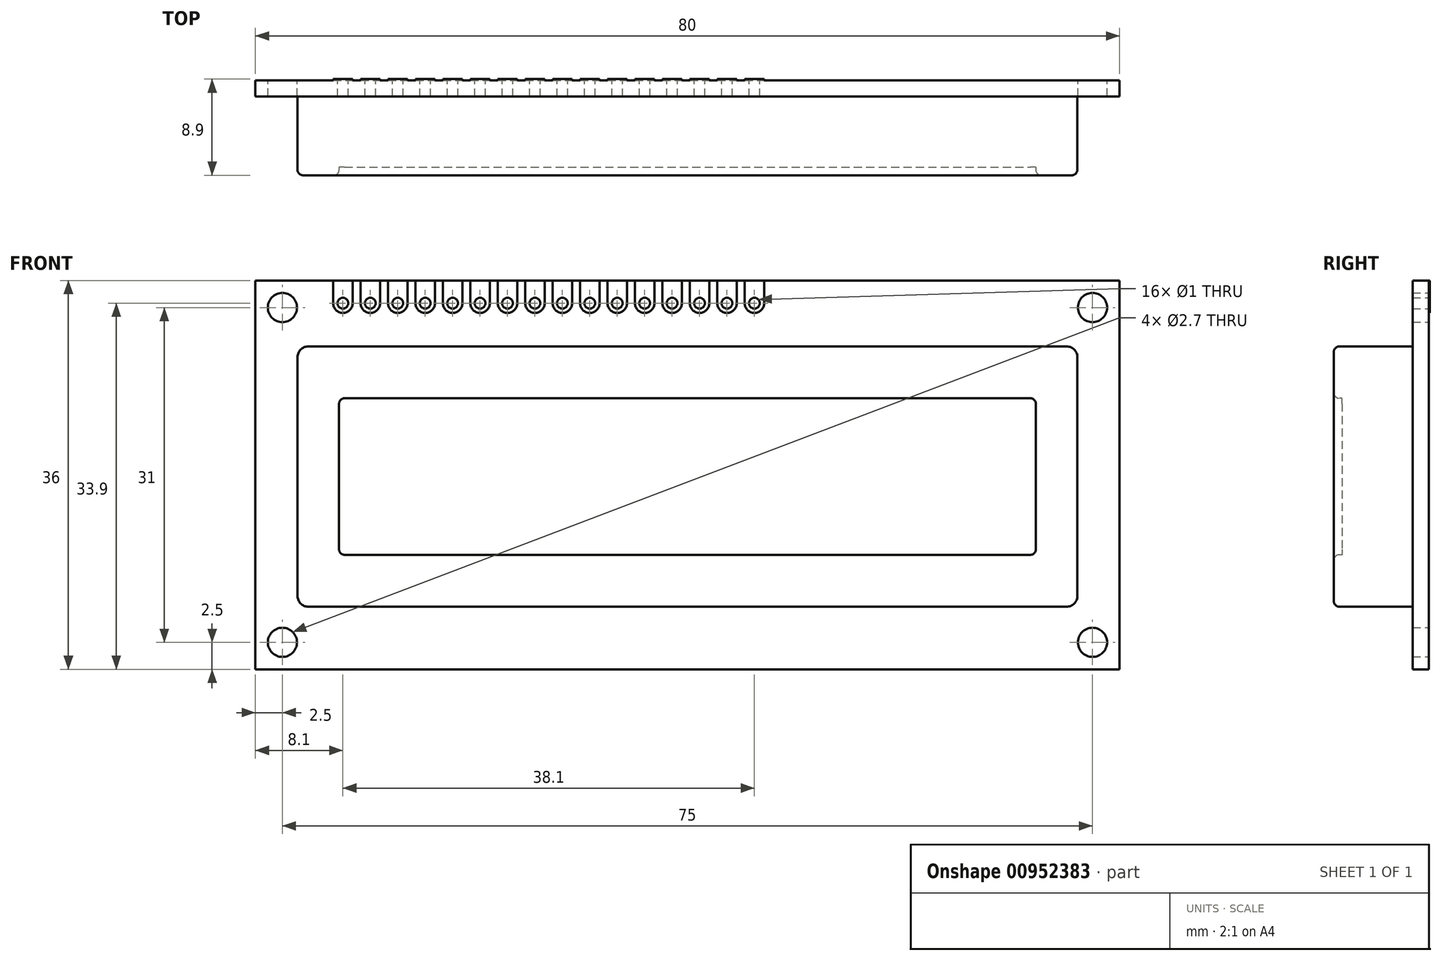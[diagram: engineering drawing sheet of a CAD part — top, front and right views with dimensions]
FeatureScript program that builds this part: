
annotation { "Feature Type Name" : "Feature", "Feature Type Description" : "" }
export const myFeature = defineFeature(function(context is Context, id is Id, definition is map)
    precondition{}
    {
        {
            var Q0;
            Q0=qCreatedBy(makeId("Front.planeOp"),FACE);
            var sketch = newSketch(context, id + "F0", { "sketchPlane" : qUnion([Q0])});
            skLineSegment(sketch, "E0.bottom", {"start": v(0, 0) * mm, "end": v(80, 0) * mm});
            skLineSegment(sketch, "E0.top", {"start": v(0, -36) * mm, "end": v(80, -36) * mm});
            skLineSegment(sketch, "E0.left", {"start": v(0, 0) * mm, "end": v(0, -36) * mm});
            skLineSegment(sketch, "E0.right", {"start": v(80, 0) * mm, "end": v(80, -36) * mm});
            skCircle(sketch, "E1", {"center": v(2.5, -2.5) * mm, "radius": 1.35 * mm});
            skCircle(sketch, "E2", {"center": v(77.5, -2.5) * mm, "radius": 1.35 * mm});
            skCircle(sketch, "E3", {"center": v(77.5, -33.5) * mm, "radius": 1.35 * mm});
            skCircle(sketch, "E4", {"center": v(2.5, -33.5) * mm, "radius": 1.35 * mm});
            skCircle(sketch, "E5", {"center": v(8.1, -2.1) * mm, "radius": 0.5 * mm});
            skCircle(sketch, "E6.1.0.0", {"center": v(10.64, -2.1) * mm, "radius": 0.5 * mm});
            skCircle(sketch, "E6.2.0.0", {"center": v(13.18, -2.1) * mm, "radius": 0.5 * mm});
            skCircle(sketch, "E6.3.0.0", {"center": v(15.72, -2.1) * mm, "radius": 0.5 * mm});
            skCircle(sketch, "E6.4.0.0", {"center": v(18.26, -2.1) * mm, "radius": 0.5 * mm});
            skCircle(sketch, "E6.5.0.0", {"center": v(20.8, -2.1) * mm, "radius": 0.5 * mm});
            skCircle(sketch, "E6.6.0.0", {"center": v(23.34, -2.1) * mm, "radius": 0.5 * mm});
            skCircle(sketch, "E6.7.0.0", {"center": v(25.88, -2.1) * mm, "radius": 0.5 * mm});
            skCircle(sketch, "E6.8.0.0", {"center": v(28.42, -2.1) * mm, "radius": 0.5 * mm});
            skCircle(sketch, "E6.9.0.0", {"center": v(30.96, -2.1) * mm, "radius": 0.5 * mm});
            skCircle(sketch, "E6.10.0.0", {"center": v(33.5, -2.1) * mm, "radius": 0.5 * mm});
            skCircle(sketch, "E6.11.0.0", {"center": v(36.04, -2.1) * mm, "radius": 0.5 * mm});
            skCircle(sketch, "E6.12.0.0", {"center": v(38.58, -2.1) * mm, "radius": 0.5 * mm});
            skCircle(sketch, "E6.13.0.0", {"center": v(41.12, -2.1) * mm, "radius": 0.5 * mm});
            skCircle(sketch, "E6.14.0.0", {"center": v(43.66, -2.1) * mm, "radius": 0.5 * mm});
            skCircle(sketch, "E6.15.0.0", {"center": v(46.2, -2.1) * mm, "radius": 0.5 * mm});
            skLineSegment(sketch, "E6.direction1", {"start": v(8.1, -2.1) * mm, "end": v(10.64, -2.1) * mm, "construction": true});
            skArc(sketch, "E7", {"start": v(7.2, -2.1) * mm, "mid": v(8.1, -3) * mm, "end": v(9, -2.1) * mm});
            skLineSegment(sketch, "E8", {"start": v(8.1, -2.1) * mm, "end": v(8.1, 0) * mm, "construction": true});
            skLineSegment(sketch, "E9", {"start": v(9, -2.1) * mm, "end": v(9, 0) * mm});
            skLineSegment(sketch, "E10", {"start": v(8.1, -2.1) * mm, "end": v(6.53, -2.1) * mm, "construction": true});
            skLineSegment(sketch, "E11", {"start": v(7.2, -2.1) * mm, "end": v(7.2, 0) * mm});
            skLineSegment(sketch, "E12", {"start": v(7.2, 0) * mm, "end": v(9, 0) * mm});
            skLineSegment(sketch, "E13.1.0.0", {"start": v(9.74, 0) * mm, "end": v(11.54, 0) * mm});
            skLineSegment(sketch, "E13.1.0.1", {"start": v(9.74, -2.1) * mm, "end": v(9.74, 0) * mm});
            skLineSegment(sketch, "E13.1.0.2", {"start": v(11.54, -2.1) * mm, "end": v(11.54, 0) * mm});
            skArc(sketch, "E13.1.0.3", {"start": v(9.74, -2.1) * mm, "mid": v(10.64, -3) * mm, "end": v(11.54, -2.1) * mm});
            skLineSegment(sketch, "E13.2.0.0", {"start": v(12.28, 0) * mm, "end": v(14.08, 0) * mm});
            skLineSegment(sketch, "E13.2.0.1", {"start": v(12.28, -2.1) * mm, "end": v(12.28, 0) * mm});
            skLineSegment(sketch, "E13.2.0.2", {"start": v(14.08, -2.1) * mm, "end": v(14.08, 0) * mm});
            skArc(sketch, "E13.2.0.3", {"start": v(12.28, -2.1) * mm, "mid": v(13.18, -3) * mm, "end": v(14.08, -2.1) * mm});
            skLineSegment(sketch, "E13.3.0.0", {"start": v(14.82, 0) * mm, "end": v(16.62, 0) * mm});
            skLineSegment(sketch, "E13.3.0.1", {"start": v(14.82, -2.1) * mm, "end": v(14.82, 0) * mm});
            skLineSegment(sketch, "E13.3.0.2", {"start": v(16.62, -2.1) * mm, "end": v(16.62, 0) * mm});
            skArc(sketch, "E13.3.0.3", {"start": v(14.82, -2.1) * mm, "mid": v(15.72, -3) * mm, "end": v(16.62, -2.1) * mm});
            skLineSegment(sketch, "E13.4.0.0", {"start": v(17.36, 0) * mm, "end": v(19.16, 0) * mm});
            skLineSegment(sketch, "E13.4.0.1", {"start": v(17.36, -2.1) * mm, "end": v(17.36, 0) * mm});
            skLineSegment(sketch, "E13.4.0.2", {"start": v(19.16, -2.1) * mm, "end": v(19.16, 0) * mm});
            skArc(sketch, "E13.4.0.3", {"start": v(17.36, -2.1) * mm, "mid": v(18.26, -3) * mm, "end": v(19.16, -2.1) * mm});
            skLineSegment(sketch, "E13.5.0.0", {"start": v(19.9, 0) * mm, "end": v(21.7, 0) * mm});
            skLineSegment(sketch, "E13.5.0.1", {"start": v(19.9, -2.1) * mm, "end": v(19.9, 0) * mm});
            skLineSegment(sketch, "E13.5.0.2", {"start": v(21.7, -2.1) * mm, "end": v(21.7, 0) * mm});
            skArc(sketch, "E13.5.0.3", {"start": v(19.9, -2.1) * mm, "mid": v(20.8, -3) * mm, "end": v(21.7, -2.1) * mm});
            skLineSegment(sketch, "E13.6.0.0", {"start": v(22.44, 0) * mm, "end": v(24.24, 0) * mm});
            skLineSegment(sketch, "E13.6.0.1", {"start": v(22.44, -2.1) * mm, "end": v(22.44, 0) * mm});
            skLineSegment(sketch, "E13.6.0.2", {"start": v(24.24, -2.1) * mm, "end": v(24.24, 0) * mm});
            skArc(sketch, "E13.6.0.3", {"start": v(22.44, -2.1) * mm, "mid": v(23.34, -3) * mm, "end": v(24.24, -2.1) * mm});
            skLineSegment(sketch, "E13.7.0.0", {"start": v(24.98, 0) * mm, "end": v(26.78, 0) * mm});
            skLineSegment(sketch, "E13.7.0.1", {"start": v(24.98, -2.1) * mm, "end": v(24.98, 0) * mm});
            skLineSegment(sketch, "E13.7.0.2", {"start": v(26.78, -2.1) * mm, "end": v(26.78, 0) * mm});
            skArc(sketch, "E13.7.0.3", {"start": v(24.98, -2.1) * mm, "mid": v(25.88, -3) * mm, "end": v(26.78, -2.1) * mm});
            skLineSegment(sketch, "E13.8.0.0", {"start": v(27.52, 0) * mm, "end": v(29.32, 0) * mm});
            skLineSegment(sketch, "E13.8.0.1", {"start": v(27.52, -2.1) * mm, "end": v(27.52, 0) * mm});
            skLineSegment(sketch, "E13.8.0.2", {"start": v(29.32, -2.1) * mm, "end": v(29.32, 0) * mm});
            skArc(sketch, "E13.8.0.3", {"start": v(27.52, -2.1) * mm, "mid": v(28.42, -3) * mm, "end": v(29.32, -2.1) * mm});
            skLineSegment(sketch, "E13.9.0.0", {"start": v(30.06, 0) * mm, "end": v(31.86, 0) * mm});
            skLineSegment(sketch, "E13.9.0.1", {"start": v(30.06, -2.1) * mm, "end": v(30.06, 0) * mm});
            skLineSegment(sketch, "E13.9.0.2", {"start": v(31.86, -2.1) * mm, "end": v(31.86, 0) * mm});
            skArc(sketch, "E13.9.0.3", {"start": v(30.06, -2.1) * mm, "mid": v(30.96, -3) * mm, "end": v(31.86, -2.1) * mm});
            skLineSegment(sketch, "E13.10.0.0", {"start": v(32.6, 0) * mm, "end": v(34.4, 0) * mm});
            skLineSegment(sketch, "E13.10.0.1", {"start": v(32.6, -2.1) * mm, "end": v(32.6, 0) * mm});
            skLineSegment(sketch, "E13.10.0.2", {"start": v(34.4, -2.1) * mm, "end": v(34.4, 0) * mm});
            skArc(sketch, "E13.10.0.3", {"start": v(32.6, -2.1) * mm, "mid": v(33.5, -3) * mm, "end": v(34.4, -2.1) * mm});
            skLineSegment(sketch, "E13.11.0.0", {"start": v(35.14, 0) * mm, "end": v(36.94, 0) * mm});
            skLineSegment(sketch, "E13.11.0.1", {"start": v(35.14, -2.1) * mm, "end": v(35.14, 0) * mm});
            skLineSegment(sketch, "E13.11.0.2", {"start": v(36.94, -2.1) * mm, "end": v(36.94, 0) * mm});
            skArc(sketch, "E13.11.0.3", {"start": v(35.14, -2.1) * mm, "mid": v(36.04, -3) * mm, "end": v(36.94, -2.1) * mm});
            skLineSegment(sketch, "E13.12.0.0", {"start": v(37.68, 0) * mm, "end": v(39.48, 0) * mm});
            skLineSegment(sketch, "E13.12.0.1", {"start": v(37.68, -2.1) * mm, "end": v(37.68, 0) * mm});
            skLineSegment(sketch, "E13.12.0.2", {"start": v(39.48, -2.1) * mm, "end": v(39.48, 0) * mm});
            skArc(sketch, "E13.12.0.3", {"start": v(37.68, -2.1) * mm, "mid": v(38.58, -3) * mm, "end": v(39.48, -2.1) * mm});
            skLineSegment(sketch, "E13.13.0.0", {"start": v(40.22, 0) * mm, "end": v(42.02, 0) * mm});
            skLineSegment(sketch, "E13.13.0.1", {"start": v(40.22, -2.1) * mm, "end": v(40.22, 0) * mm});
            skLineSegment(sketch, "E13.13.0.2", {"start": v(42.02, -2.1) * mm, "end": v(42.02, 0) * mm});
            skArc(sketch, "E13.13.0.3", {"start": v(40.22, -2.1) * mm, "mid": v(41.12, -3) * mm, "end": v(42.02, -2.1) * mm});
            skLineSegment(sketch, "E13.14.0.0", {"start": v(42.76, 0) * mm, "end": v(44.56, 0) * mm});
            skLineSegment(sketch, "E13.14.0.1", {"start": v(42.76, -2.1) * mm, "end": v(42.76, 0) * mm});
            skLineSegment(sketch, "E13.14.0.2", {"start": v(44.56, -2.1) * mm, "end": v(44.56, 0) * mm});
            skArc(sketch, "E13.14.0.3", {"start": v(42.76, -2.1) * mm, "mid": v(43.66, -3) * mm, "end": v(44.56, -2.1) * mm});
            skLineSegment(sketch, "E13.15.0.0", {"start": v(45.3, 0) * mm, "end": v(47.1, 0) * mm});
            skLineSegment(sketch, "E13.15.0.1", {"start": v(45.3, -2.1) * mm, "end": v(45.3, 0) * mm});
            skLineSegment(sketch, "E13.15.0.2", {"start": v(47.1, -2.1) * mm, "end": v(47.1, 0) * mm});
            skArc(sketch, "E13.15.0.3", {"start": v(45.3, -2.1) * mm, "mid": v(46.2, -3) * mm, "end": v(47.1, -2.1) * mm});
            skLineSegment(sketch, "E13.direction1", {"start": v(7.2, -2.1) * mm, "end": v(9.74, -2.1) * mm, "construction": true});
            skSolve(sketch);
        }
        {
            var Q0;
            Q0 = qSketchRegion(id + "F0", true);
            extrude(context, id + "F1", {"entities" : qUnion([Q0]), "depth" : 1.5 * mm, "offsetDistance" : 25 * mm});
        }
        {
            var Q0;
            Q0=makeQuery(id+"F1.opExtrude","CAP_FACE",FACE,{"disambiguationData":[OSD([sQuery(id+"F0.wireOp",EDGE,"E0.bottom"),sQuery(id+"F0.wireOp",EDGE,"E0.top"),sQuery(id+"F0.wireOp",EDGE,"E0.left"),sQuery(id+"F0.wireOp",EDGE,"E0.right"),sQuery(id+"F0.wireOp",EDGE,"E1"),sQuery(id+"F0.wireOp",EDGE,"E2"),sQuery(id+"F0.wireOp",EDGE,"E3"),sQuery(id+"F0.wireOp",EDGE,"E4"),sQuery(id+"F0.wireOp",EDGE,"E5"),sQuery(id+"F0.wireOp",EDGE,"E6.1.0.0"),sQuery(id+"F0.wireOp",EDGE,"E6.2.0.0"),sQuery(id+"F0.wireOp",EDGE,"E6.3.0.0"),sQuery(id+"F0.wireOp",EDGE,"E6.4.0.0"),sQuery(id+"F0.wireOp",EDGE,"E6.5.0.0"),sQuery(id+"F0.wireOp",EDGE,"E6.6.0.0"),sQuery(id+"F0.wireOp",EDGE,"E6.7.0.0"),sQuery(id+"F0.wireOp",EDGE,"E6.8.0.0"),sQuery(id+"F0.wireOp",EDGE,"E6.9.0.0"),sQuery(id+"F0.wireOp",EDGE,"E6.10.0.0"),sQuery(id+"F0.wireOp",EDGE,"E6.11.0.0"),sQuery(id+"F0.wireOp",EDGE,"E6.12.0.0"),sQuery(id+"F0.wireOp",EDGE,"E6.13.0.0"),sQuery(id+"F0.wireOp",EDGE,"E6.14.0.0"),sQuery(id+"F0.wireOp",EDGE,"E6.15.0.0")])],"isStart":false});
            var sketch = newSketch(context, id + "F2", { "sketchPlane" : qUnion([Q0])});
            skLineSegment(sketch, "E14.bottom", {"start": v(4.9, -6.1) * mm, "end": v(75.1, -6.1) * mm});
            skLineSegment(sketch, "E14.top", {"start": v(4.9, -30.2) * mm, "end": v(75.1, -30.2) * mm});
            skLineSegment(sketch, "E14.left", {"start": v(3.9, -7.1) * mm, "end": v(3.9, -29.2) * mm});
            skLineSegment(sketch, "E14.right", {"start": v(76.1, -7.1) * mm, "end": v(76.1, -29.2) * mm});
            skPoint(sketch, "E15.visualSharp", {"position": v(3.9, -6.1) * mm});
            skArc(sketch, "E15.filletArc", {"start": v(4.9, -6.1) * mm, "mid": v(4.2, -6.4) * mm, "end": v(3.9, -7.1) * mm});
            skPoint(sketch, "E16.visualSharp", {"position": v(76.1, -6.1) * mm});
            skArc(sketch, "E16.filletArc", {"start": v(76.1, -7.1) * mm, "mid": v(75.8, -6.4) * mm, "end": v(75.1, -6.1) * mm});
            skPoint(sketch, "E17.visualSharp", {"position": v(76.1, -30.2) * mm});
            skArc(sketch, "E17.filletArc", {"start": v(75.1, -30.2) * mm, "mid": v(75.8, -29.9) * mm, "end": v(76.1, -29.2) * mm});
            skPoint(sketch, "E18.visualSharp", {"position": v(3.9, -30.2) * mm});
            skArc(sketch, "E18.filletArc", {"start": v(3.9, -29.2) * mm, "mid": v(4.2, -29.9) * mm, "end": v(4.9, -30.2) * mm});
            skSolve(sketch);
        }
        {
            var Q0;
            Q0=makeQuery(id+"F2.imprint","IMPRINT",FACE,{"disambiguationData":[TD([[makeQuery(id+"F2.imprint","IMPRINT",EDGE,{"derivedFrom":sQuery(id+"F2.wireOp",EDGE,"E14.bottom")}),-1.0]])]});
            extrude(context, id + "F3", {"entities" : qUnion([Q0]), "operationType" : NewBodyOperationType.ADD, "depth" : 7.3 * mm, "offsetDistance" : 25 * mm});
        }
        {
            var Q0;
            Q0=makeQuery(id+"F3.opExtrude","CAP_FACE",FACE,{"disambiguationData":[OSD([sQuery(id+"F2.wireOp",EDGE,"E14.bottom"),sQuery(id+"F2.wireOp",EDGE,"E14.top"),sQuery(id+"F2.wireOp",EDGE,"E14.left"),sQuery(id+"F2.wireOp",EDGE,"E14.right"),sQuery(id+"F2.wireOp",EDGE,"E15.filletArc"),sQuery(id+"F2.wireOp",EDGE,"E16.filletArc"),sQuery(id+"F2.wireOp",EDGE,"E17.filletArc"),sQuery(id+"F2.wireOp",EDGE,"E18.filletArc")])],"isStart":false});
            var sketch = newSketch(context, id + "F4", { "sketchPlane" : qUnion([Q0])});
            skLineSegment(sketch, "E19.bottom", {"start": v(8.25, -10.9) * mm, "end": v(71.75, -10.9) * mm});
            skLineSegment(sketch, "E19.top", {"start": v(8.25, -25.4) * mm, "end": v(71.75, -25.4) * mm});
            skLineSegment(sketch, "E19.left", {"start": v(7.75, -11.4) * mm, "end": v(7.75, -24.9) * mm});
            skLineSegment(sketch, "E19.right", {"start": v(72.25, -11.4) * mm, "end": v(72.25, -24.9) * mm});
            skPoint(sketch, "E20.visualSharp", {"position": v(7.75, -10.9) * mm});
            skArc(sketch, "E20.filletArc", {"start": v(8.25, -10.9) * mm, "mid": v(7.9, -11.05) * mm, "end": v(7.75, -11.4) * mm});
            skPoint(sketch, "E21.visualSharp", {"position": v(72.25, -10.9) * mm});
            skArc(sketch, "E21.filletArc", {"start": v(72.25, -11.4) * mm, "mid": v(72.1, -11.05) * mm, "end": v(71.75, -10.9) * mm});
            skPoint(sketch, "E22.visualSharp", {"position": v(72.25, -25.4) * mm});
            skArc(sketch, "E22.filletArc", {"start": v(71.75, -25.4) * mm, "mid": v(72.1, -25.25) * mm, "end": v(72.25, -24.9) * mm});
            skPoint(sketch, "E23.visualSharp", {"position": v(7.75, -25.4) * mm});
            skArc(sketch, "E23.filletArc", {"start": v(7.75, -24.9) * mm, "mid": v(7.9, -25.25) * mm, "end": v(8.25, -25.4) * mm});
            skSolve(sketch);
        }
        {
            var Q0;
            Q0=makeQuery(id+"F4.imprint","IMPRINT",FACE,{"disambiguationData":[TD([[makeQuery(id+"F4.imprint","IMPRINT",EDGE,{"derivedFrom":sQuery(id+"F4.wireOp",EDGE,"E19.bottom")}),-1.0]])]});
            extrude(context, id + "F5", {"entities" : qUnion([Q0]), "operationType" : NewBodyOperationType.REMOVE, "oppositeDirection" : true, "depth" : 0.75 * mm, "offsetDistance" : 25 * mm});
        }
        {
            var Q0;
            Q0=makeQuery(id+"F3.opExtrude","CAP_FACE",FACE,{"disambiguationData":[OSD([sQuery(id+"F2.wireOp",EDGE,"E14.bottom"),sQuery(id+"F2.wireOp",EDGE,"E14.top"),sQuery(id+"F2.wireOp",EDGE,"E14.left"),sQuery(id+"F2.wireOp",EDGE,"E14.right"),sQuery(id+"F2.wireOp",EDGE,"E15.filletArc"),sQuery(id+"F2.wireOp",EDGE,"E16.filletArc"),sQuery(id+"F2.wireOp",EDGE,"E17.filletArc"),sQuery(id+"F2.wireOp",EDGE,"E18.filletArc")])],"isStart":false});
            fillet(context, id + "F6", {"entities" : qUnion([Q0]), "radius" : 0.5 * mm, "tangentPropagation" : true, "allowEdgeOverflow" : false});
        }
        {
            var Q0;
            Q0=makeQuery(id+"F0.imprint","IMPRINT",FACE,{"disambiguationData":[TD([[makeQuery(id+"F0.imprint","IMPRINT",EDGE,{"derivedFrom":sQuery(id+"F0.wireOp",EDGE,"E5")}),-1.0]])]});
            var Q1;
            Q1=makeQuery(id+"F0.imprint","IMPRINT",FACE,{"disambiguationData":[TD([[makeQuery(id+"F0.imprint","IMPRINT",EDGE,{"derivedFrom":sQuery(id+"F0.wireOp",EDGE,"E6.1.0.0")}),-1.0]])]});
            var Q2;
            Q2=makeQuery(id+"F0.imprint","IMPRINT",FACE,{"disambiguationData":[TD([[makeQuery(id+"F0.imprint","IMPRINT",EDGE,{"derivedFrom":sQuery(id+"F0.wireOp",EDGE,"E6.2.0.0")}),-1.0]])]});
            var Q3;
            Q3=makeQuery(id+"F0.imprint","IMPRINT",FACE,{"disambiguationData":[TD([[makeQuery(id+"F0.imprint","IMPRINT",EDGE,{"derivedFrom":sQuery(id+"F0.wireOp",EDGE,"E6.3.0.0")}),-1.0]])]});
            var Q4;
            Q4=makeQuery(id+"F0.imprint","IMPRINT",FACE,{"disambiguationData":[TD([[makeQuery(id+"F0.imprint","IMPRINT",EDGE,{"derivedFrom":sQuery(id+"F0.wireOp",EDGE,"E6.4.0.0")}),-1.0]])]});
            var Q5;
            Q5=makeQuery(id+"F0.imprint","IMPRINT",FACE,{"disambiguationData":[TD([[makeQuery(id+"F0.imprint","IMPRINT",EDGE,{"derivedFrom":sQuery(id+"F0.wireOp",EDGE,"E6.5.0.0")}),-1.0]])]});
            var Q6;
            Q6=makeQuery(id+"F0.imprint","IMPRINT",FACE,{"disambiguationData":[TD([[makeQuery(id+"F0.imprint","IMPRINT",EDGE,{"derivedFrom":sQuery(id+"F0.wireOp",EDGE,"E6.6.0.0")}),-1.0]])]});
            var Q7;
            Q7=makeQuery(id+"F0.imprint","IMPRINT",FACE,{"disambiguationData":[TD([[makeQuery(id+"F0.imprint","IMPRINT",EDGE,{"derivedFrom":sQuery(id+"F0.wireOp",EDGE,"E6.7.0.0")}),-1.0]])]});
            var Q8;
            Q8=makeQuery(id+"F0.imprint","IMPRINT",FACE,{"disambiguationData":[TD([[makeQuery(id+"F0.imprint","IMPRINT",EDGE,{"derivedFrom":sQuery(id+"F0.wireOp",EDGE,"E6.8.0.0")}),-1.0]])]});
            var Q9;
            Q9=makeQuery(id+"F0.imprint","IMPRINT",FACE,{"disambiguationData":[TD([[makeQuery(id+"F0.imprint","IMPRINT",EDGE,{"derivedFrom":sQuery(id+"F0.wireOp",EDGE,"E6.9.0.0")}),-1.0]])]});
            var Q10;
            Q10=makeQuery(id+"F0.imprint","IMPRINT",FACE,{"disambiguationData":[TD([[makeQuery(id+"F0.imprint","IMPRINT",EDGE,{"derivedFrom":sQuery(id+"F0.wireOp",EDGE,"E6.10.0.0")}),-1.0]])]});
            var Q11;
            Q11=makeQuery(id+"F0.imprint","IMPRINT",FACE,{"disambiguationData":[TD([[makeQuery(id+"F0.imprint","IMPRINT",EDGE,{"derivedFrom":sQuery(id+"F0.wireOp",EDGE,"E6.11.0.0")}),-1.0]])]});
            var Q12;
            Q12=makeQuery(id+"F0.imprint","IMPRINT",FACE,{"disambiguationData":[TD([[makeQuery(id+"F0.imprint","IMPRINT",EDGE,{"derivedFrom":sQuery(id+"F0.wireOp",EDGE,"E6.12.0.0")}),-1.0]])]});
            var Q13;
            Q13=makeQuery(id+"F0.imprint","IMPRINT",FACE,{"disambiguationData":[TD([[makeQuery(id+"F0.imprint","IMPRINT",EDGE,{"derivedFrom":sQuery(id+"F0.wireOp",EDGE,"E6.13.0.0")}),-1.0]])]});
            var Q14;
            Q14=makeQuery(id+"F0.imprint","IMPRINT",FACE,{"disambiguationData":[TD([[makeQuery(id+"F0.imprint","IMPRINT",EDGE,{"derivedFrom":sQuery(id+"F0.wireOp",EDGE,"E6.14.0.0")}),-1.0]])]});
            var Q15;
            Q15=makeQuery(id+"F0.imprint","IMPRINT",FACE,{"disambiguationData":[TD([[makeQuery(id+"F0.imprint","IMPRINT",EDGE,{"derivedFrom":sQuery(id+"F0.wireOp",EDGE,"E6.15.0.0")}),-1.0]])]});
            extrude(context, id + "F7", {"entities" : qUnion([Q0, Q1, Q2, Q3, Q4, Q5, Q6, Q7, Q8, Q9, Q10, Q11, Q12, Q13, Q14, Q15]), "operationType" : NewBodyOperationType.ADD, "depth" : 1.51 * mm, "offsetDistance" : 25 * mm});
        }
        {
            var Q0;
            Q0=makeQuery(id+"F0.imprint","IMPRINT",FACE,{"disambiguationData":[TD([[makeQuery(id+"F0.imprint","IMPRINT",EDGE,{"derivedFrom":sQuery(id+"F0.wireOp",EDGE,"E5")}),-1.0]])]});
            var Q1;
            Q1=makeQuery(id+"F0.imprint","IMPRINT",FACE,{"disambiguationData":[TD([[makeQuery(id+"F0.imprint","IMPRINT",EDGE,{"derivedFrom":sQuery(id+"F0.wireOp",EDGE,"E6.1.0.0")}),-1.0]])]});
            var Q2;
            Q2=makeQuery(id+"F0.imprint","IMPRINT",FACE,{"disambiguationData":[TD([[makeQuery(id+"F0.imprint","IMPRINT",EDGE,{"derivedFrom":sQuery(id+"F0.wireOp",EDGE,"E6.2.0.0")}),-1.0]])]});
            var Q3;
            Q3=makeQuery(id+"F0.imprint","IMPRINT",FACE,{"disambiguationData":[TD([[makeQuery(id+"F0.imprint","IMPRINT",EDGE,{"derivedFrom":sQuery(id+"F0.wireOp",EDGE,"E6.3.0.0")}),-1.0]])]});
            var Q4;
            Q4=makeQuery(id+"F0.imprint","IMPRINT",FACE,{"disambiguationData":[TD([[makeQuery(id+"F0.imprint","IMPRINT",EDGE,{"derivedFrom":sQuery(id+"F0.wireOp",EDGE,"E6.4.0.0")}),-1.0]])]});
            var Q5;
            Q5=makeQuery(id+"F0.imprint","IMPRINT",FACE,{"disambiguationData":[TD([[makeQuery(id+"F0.imprint","IMPRINT",EDGE,{"derivedFrom":sQuery(id+"F0.wireOp",EDGE,"E6.5.0.0")}),-1.0]])]});
            var Q6;
            Q6=makeQuery(id+"F0.imprint","IMPRINT",FACE,{"disambiguationData":[TD([[makeQuery(id+"F0.imprint","IMPRINT",EDGE,{"derivedFrom":sQuery(id+"F0.wireOp",EDGE,"E6.6.0.0")}),-1.0]])]});
            var Q7;
            Q7=makeQuery(id+"F0.imprint","IMPRINT",FACE,{"disambiguationData":[TD([[makeQuery(id+"F0.imprint","IMPRINT",EDGE,{"derivedFrom":sQuery(id+"F0.wireOp",EDGE,"E6.7.0.0")}),-1.0]])]});
            var Q8;
            Q8=makeQuery(id+"F0.imprint","IMPRINT",FACE,{"disambiguationData":[TD([[makeQuery(id+"F0.imprint","IMPRINT",EDGE,{"derivedFrom":sQuery(id+"F0.wireOp",EDGE,"E6.8.0.0")}),-1.0]])]});
            var Q9;
            Q9=makeQuery(id+"F0.imprint","IMPRINT",FACE,{"disambiguationData":[TD([[makeQuery(id+"F0.imprint","IMPRINT",EDGE,{"derivedFrom":sQuery(id+"F0.wireOp",EDGE,"E6.9.0.0")}),-1.0]])]});
            var Q10;
            Q10=makeQuery(id+"F0.imprint","IMPRINT",FACE,{"disambiguationData":[TD([[makeQuery(id+"F0.imprint","IMPRINT",EDGE,{"derivedFrom":sQuery(id+"F0.wireOp",EDGE,"E6.10.0.0")}),-1.0]])]});
            var Q11;
            Q11=makeQuery(id+"F0.imprint","IMPRINT",FACE,{"disambiguationData":[TD([[makeQuery(id+"F0.imprint","IMPRINT",EDGE,{"derivedFrom":sQuery(id+"F0.wireOp",EDGE,"E6.11.0.0")}),-1.0]])]});
            var Q12;
            Q12=makeQuery(id+"F0.imprint","IMPRINT",FACE,{"disambiguationData":[TD([[makeQuery(id+"F0.imprint","IMPRINT",EDGE,{"derivedFrom":sQuery(id+"F0.wireOp",EDGE,"E6.12.0.0")}),-1.0]])]});
            var Q13;
            Q13=makeQuery(id+"F0.imprint","IMPRINT",FACE,{"disambiguationData":[TD([[makeQuery(id+"F0.imprint","IMPRINT",EDGE,{"derivedFrom":sQuery(id+"F0.wireOp",EDGE,"E6.13.0.0")}),-1.0]])]});
            var Q14;
            Q14=makeQuery(id+"F0.imprint","IMPRINT",FACE,{"disambiguationData":[TD([[makeQuery(id+"F0.imprint","IMPRINT",EDGE,{"derivedFrom":sQuery(id+"F0.wireOp",EDGE,"E6.14.0.0")}),-1.0]])]});
            var Q15;
            Q15=makeQuery(id+"F0.imprint","IMPRINT",FACE,{"disambiguationData":[TD([[makeQuery(id+"F0.imprint","IMPRINT",EDGE,{"derivedFrom":sQuery(id+"F0.wireOp",EDGE,"E6.15.0.0")}),-1.0]])]});
            extrude(context, id + "F8", {"entities" : qUnion([Q0, Q1, Q2, Q3, Q4, Q5, Q6, Q7, Q8, Q9, Q10, Q11, Q12, Q13, Q14, Q15]), "operationType" : NewBodyOperationType.ADD, "oppositeDirection" : true, "depth" : 0.1 * mm, "offsetDistance" : 25 * mm});
        }
    });
